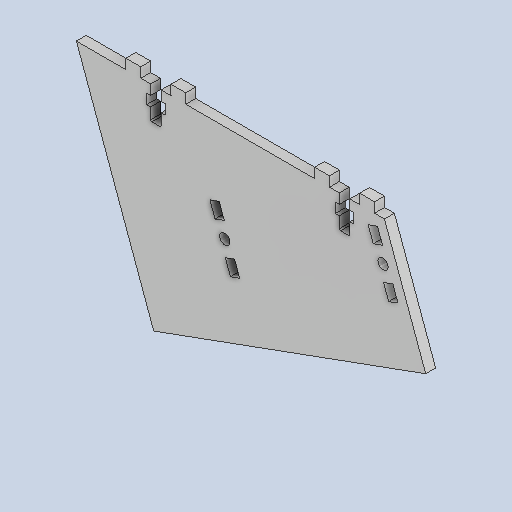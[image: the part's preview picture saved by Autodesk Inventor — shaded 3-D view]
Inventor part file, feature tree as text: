
AUTODESK INVENTOR PART (.ipt)
format: ipt  version: 2024.1 (Build 281209000, 209)  size: 390,144 bytes
history: native  units: mm
features: other x9, extrude x1, sketch x1
ambient origin geometry x8: Origin, YZ Plane, XZ Plane, XY Plane, X Axis, Y Axis, Z Axis, Center Point
bodies: Solide1 (feature_tree)
feature tree (11):
  other  "shared_parameters.ipt"
  other  "tc_base_plate.ipt"
  other  "Blocs"
  extrude  "Extrusion1"  Depth=10.0mm
  other  "Anchor (screw side)"
  other  "Anchor (nut side)"
  sketch  "Esquisse1"
  other  "Anchor (nut side):1"
  other  "Anchor (nut side):2"
  other  "Anchor (screw side):2"
  other  "Anchor (screw side):3"
